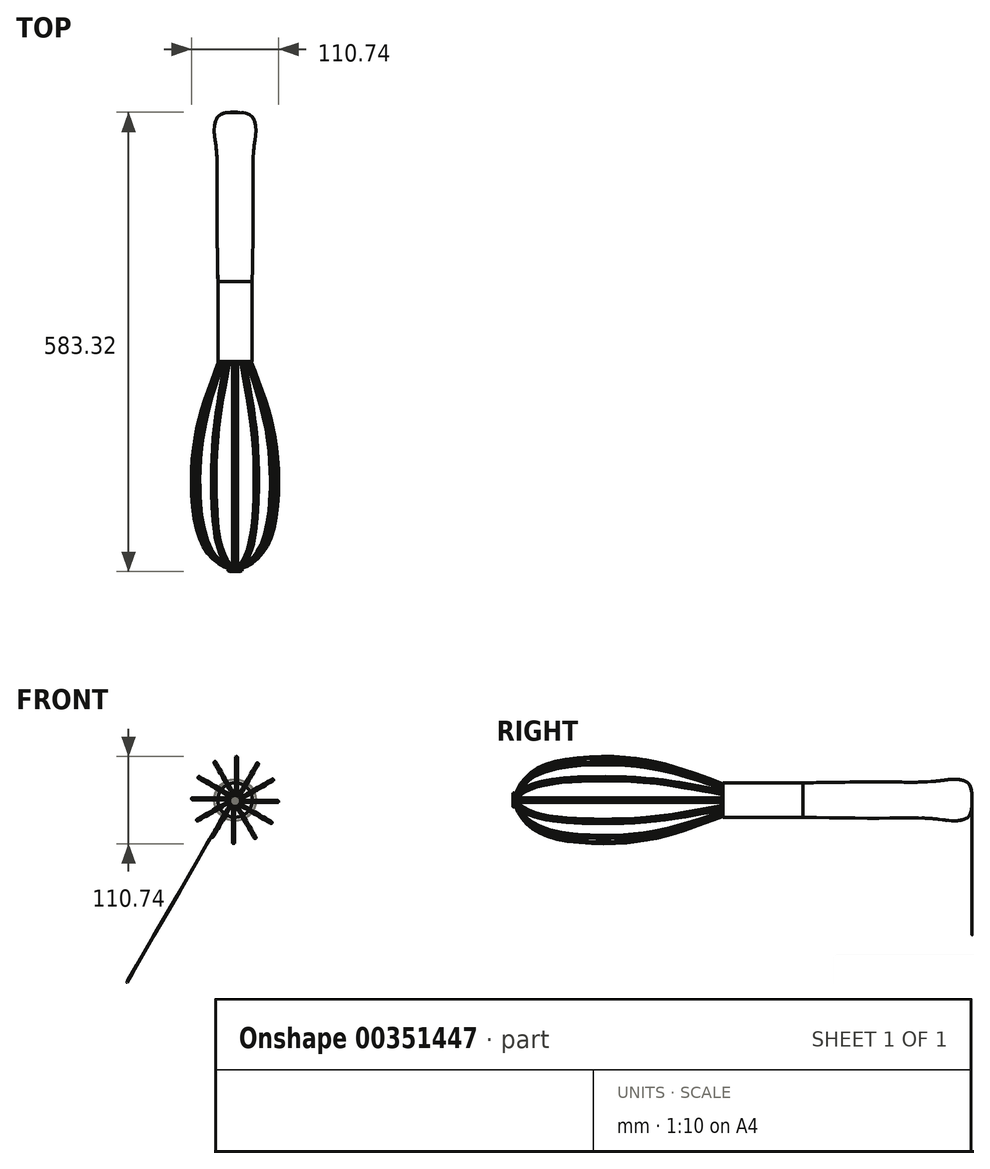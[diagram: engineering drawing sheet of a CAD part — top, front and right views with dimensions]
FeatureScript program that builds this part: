
annotation { "Feature Type Name" : "Feature", "Feature Type Description" : "" }
export const myFeature = defineFeature(function(context is Context, id is Id, definition is map)
    precondition{}
    {
        {
            var Q0;
            Q0=qCreatedBy(makeId("Top.planeOp"),FACE);
            var sketch = newSketch(context, id + "F0", { "sketchPlane" : qUnion([Q0])});
            skFitSpline(sketch, "E0", {"points": [v(-21.83, 0) * mm, v(-23, 99.17) * mm, v(-22.97, 154.53) * mm, v(-25.1, 178.11) * mm, v(-26.48, 192.4) * mm, v(-23.55, 206.79) * mm, v(-16.03, 213.27) * mm, v(0, 214.72) * mm, v(6.8, 214.25) * mm], "startDerivative": vector(-7.71, 416.82) * mm, "endDerivative": vector(88.06, -8.5) * mm});
            skLineSegment(sketch, "E1", {"start": v(-21.83, 0) * mm, "end": v(0, 0) * mm});
            skLineSegment(sketch, "E2", {"start": v(0, 0) * mm, "end": v(0, 214.72) * mm});
            skSolve(sketch);
        }
        {
            var Q0;
            Q0 = qSketchRegion(id + "F0", true);
            var Q1;
            Q1=sQuery(id+"F0.wireOp",EDGE,"E2");
            revolve(context, id + "F1", {"entities" : qUnion([Q0]), "axis" : qUnion([Q1]), "revolveType" : RevolveType.FULL});
        }
        {
            var Q0;
            Q0=makeQuery(id+"F1.opRevolve","SWEPT_FACE",FACE,{"disambiguationData":[OSD([sQuery(id+"F0.wireOp",EDGE,"E1")])]});
            extrude(context, id + "F2", {"entities" : qUnion([Q0]), "operationType" : NewBodyOperationType.ADD, "depth" : 101.6 * mm});
        }
        {
            var Q0;
            Q0=qCreatedBy(makeId("Right.planeOp"),FACE);
            var sketch = newSketch(context, id + "F3", { "sketchPlane" : qUnion([Q0])});
            skFitSpline(sketch, "E3", {"points": [v(-105.02, -19.45) * mm, v(-168.42, -41.6) * mm, v(-231.9, -52.43) * mm, v(-318.72, -45.6) * mm, v(-353.94, -23.22) * mm, v(-364.93, 0) * mm, v(-365.55, 11.48) * mm], "startDerivative": vector(-317.65, -120.34) * mm, "endDerivative": vector(5.13, 125.34) * mm});
            skLineSegment(sketch, "E4", {"start": v(-102.5, 0) * mm, "end": v(-365.7, 7.98) * mm, "construction": true});
            skPoint(sketch, "E5.MirrorCS.0.internal.orphan", {"position": v(-103.84, 19.57) * mm});
            skPoint(sketch, "E5.MirrorCS.end.orphan", {"position": v(-365.76, 4.48) * mm});
            skSolve(sketch);
        }
        {
            var Q0;
            Q0=makeQuery(id+"F2.opExtrude","CAP_FACE",FACE,{"disambiguationData":[OSD([sQuery(id+"F0.wireOp",EDGE,"E1")])],"isStart":false});
            var sketch = newSketch(context, id + "F4", { "sketchPlane" : qUnion([Q0])});
            skCircle(sketch, "E6", {"center": v(-0.25, 19.26) * mm, "radius": 1.27 * mm});
            skCircle(sketch, "E7", {"center": v(-1.78, -19.34) * mm, "radius": 1.27 * mm});
            skSolve(sketch);
        }
        {
            var Q0;
            Q0=makeQuery(id+"F4.imprint","IMPRINT",FACE,{"disambiguationData":[TD([[makeQuery(id+"F4.imprint","IMPRINT",EDGE,{"derivedFrom":sQuery(id+"F4.wireOp",EDGE,"E7")}),1.0]])]});
            var Q1;
            Q1=sQuery(id+"F3.wireOp",EDGE,"E3");
            sweep(context, id + "F5", {"operationType" : NewBodyOperationType.ADD, "profiles" : qUnion([Q0]), "path" : qUnion([Q1])});
        }
        {
            var Q0;
            Q0=makeQuery(id+"F1.opRevolve","SWEPT_BODY",BODY,{"disambiguationData":[OSD([sQuery(id+"F0.wireOp",EDGE,"E0"),sQuery(id+"F0.wireOp",EDGE,"E1"),sQuery(id+"F0.wireOp",EDGE,"E2")])]});
            var Q1;
            Q1=makeQuery(id+"F2.opExtrude","CAP_EDGE",EDGE,{"disambiguationData":[OSD([sQuery(id+"F0.wireOp",EDGE,"E0"),sQuery(id+"F0.wireOp",EDGE,"E1")])],"isStart":false});
            circularPattern(context, id + "F6", {"entities" : qUnion([Q0]), "axis" : qUnion([Q1]), "angle" : 360 * degree, "instanceCount" : 12, "oppositeDirection" : true, "equalSpace" : true});
        }
        {
            var Q0;
            Q0=makeQuery(id+"F6.opPattern","COPY",FACE,{"derivedFrom":makeQuery(id+"F2.opExtrude","CAP_FACE",FACE,{"disambiguationData":[OSD([sQuery(id+"F0.wireOp",EDGE,"E1")])],"isStart":false}),"instanceName":"4"});
            cPlane(context, id + "F7", {"entities" : qUnion([Q0]), "cplaneType" : CPlaneType.OFFSET, "offset" : 262.38 * mm, "width" : 152.4 * mm, "height" : 152.4 * mm});
        }
        {
            var Q0;
            Q0=qCreatedBy(id+"F7.planeOp",FACE);
            var sketch = newSketch(context, id + "F8", { "sketchPlane" : qUnion([Q0])});
            skCircle(sketch, "E8", {"center": v(0, -1.14) * mm, "radius": 6.99 * mm});
            skSolve(sketch);
        }
        {
            var Q0;
            Q0=makeQuery(id+"F8.imprint","IMPRINT",FACE,{"disambiguationData":[TD([[makeQuery(id+"F8.imprint","IMPRINT",EDGE,{"derivedFrom":sQuery(id+"F8.wireOp",EDGE,"E8")}),1.0]])]});
            extrude(context, id + "F9", {"entities" : qUnion([Q0]), "depth" : 4.57 * mm});
        }
    });
